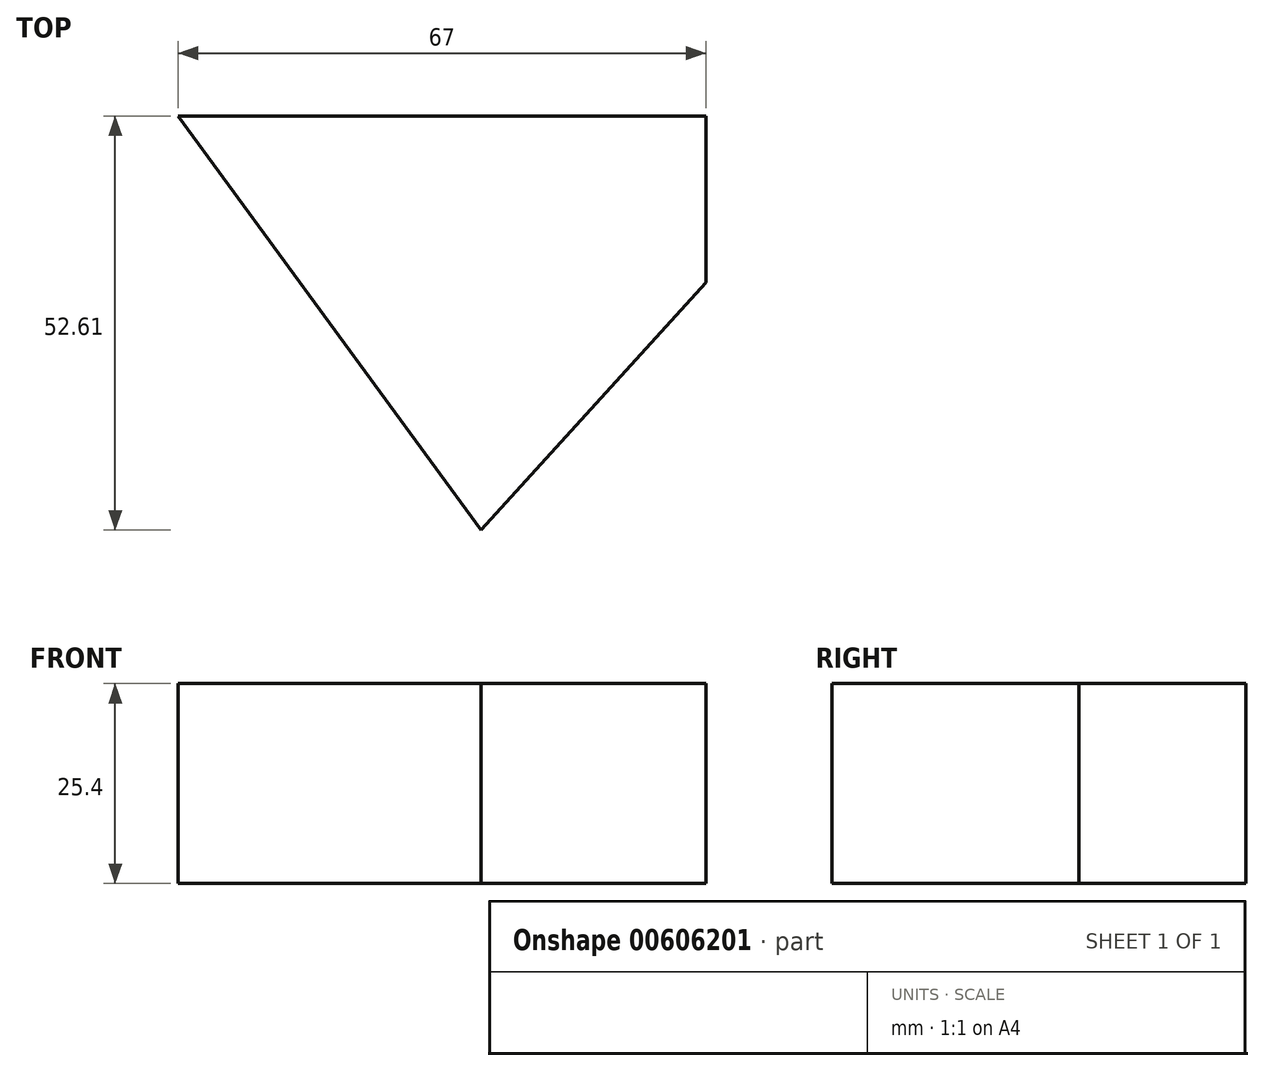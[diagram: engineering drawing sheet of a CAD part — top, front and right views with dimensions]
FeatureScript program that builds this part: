
annotation { "Feature Type Name" : "Feature", "Feature Type Description" : "" }
export const myFeature = defineFeature(function(context is Context, id is Id, definition is map)
    precondition{}
    {
        {
            var Q0;
            Q0=qCreatedBy(makeId("Top.planeOp"),FACE);
            var sketch = newSketch(context, id + "F0", { "sketchPlane" : qUnion([Q0])});
            skLineSegment(sketch, "E0", {"start": v(0, 0) * mm, "end": v(20.2, 0) * mm});
            skLineSegment(sketch, "E1", {"start": v(20.2, 0) * mm, "end": v(20.2, 21.18) * mm});
            skLineSegment(sketch, "E2", {"start": v(20.2, 21.18) * mm, "end": v(-46.8, 21.18) * mm});
            skLineSegment(sketch, "E3", {"start": v(-46.8, 21.18) * mm, "end": v(-8.38, -31.43) * mm});
            skLineSegment(sketch, "E4", {"start": v(-8.38, -31.43) * mm, "end": v(20.2, 0) * mm});
            skSolve(sketch);
        }
        {
            var Q0;
            Q0 = qSketchRegion(id + "F0", true);
            extrude(context, id + "F1", {"entities" : qUnion([Q0]), "depth" : 25.4 * mm, "offsetDistance" : 25.4 * mm});
        }
    });
